# Revit family: BIMLIB_ПланкаУглаВнутреннего_GRANDLINE
name_source: partatom
category: Обобщенные модели
revit_build: Autodesk Revit 2017 (Build: 20170118_1100(x64)
units: mm (PartAtom-declared; Revit-internal decimal feet)

## family parameters
Может служить основой для арматурных стержней = Нет
Общий = Нет
При загрузке вырезать с полостями = Нет
Размер круглого соединителя = Использовать диаметр
Тип детали = Нормальный
Точка расчета площади = Нет

## types (5) — shared parameters
ADSK_URL документации изделия = https://www.grandline.ru
ADSK_URL страницы изделия = https://www.grandline.ru
ADSK_Версия Revit = 2017
ADSK_Группирование = Доборные элементы
ADSK_Единица измерения = м
ADSK_Завод-изготовитель = Grand Line
ADSK_Материал = GL_Drap_RAL7016
ADSK_Материал тип подсчета = 1
ADSK_Обозначение = ГОСТ 19904-90, ГОСТ 14918-80
BL_BIM library = https://bimlib.pro
URL = https://www.grandline.ru
Изготовитель = Grand Line

## per-type parameters (varying)
| type | ADSK_Код изделия | ADSK_Наименование | ADSK_Размер_Глубина | Нахлест_Длина | Описание |
| 30х30 | M011-056 | Планка угла внутреннего 30х30 | 30 мм | 10 мм | Планка угла внутреннего 30х30 |
| 40х40 | M018.060.002 | Угол внутренний 40х40 | 40 мм | 10 мм | Угол внутренний 40х40 |
| 50х50 | M011-057 | Планка угла внутреннего 50х50 | 50 мм | 13 мм | Планка угла внутреннего 50х50 |
| 70х70 | M018.060.001 | Угол внутренний 70х70 | 70 мм | 10 мм | Угол внутренний 70х70 |
| 110х110 | M011-058 | Планка угла внутреннего 110х110 | 50 мм | 15 мм | Планка угла внутреннего 110х110 |
